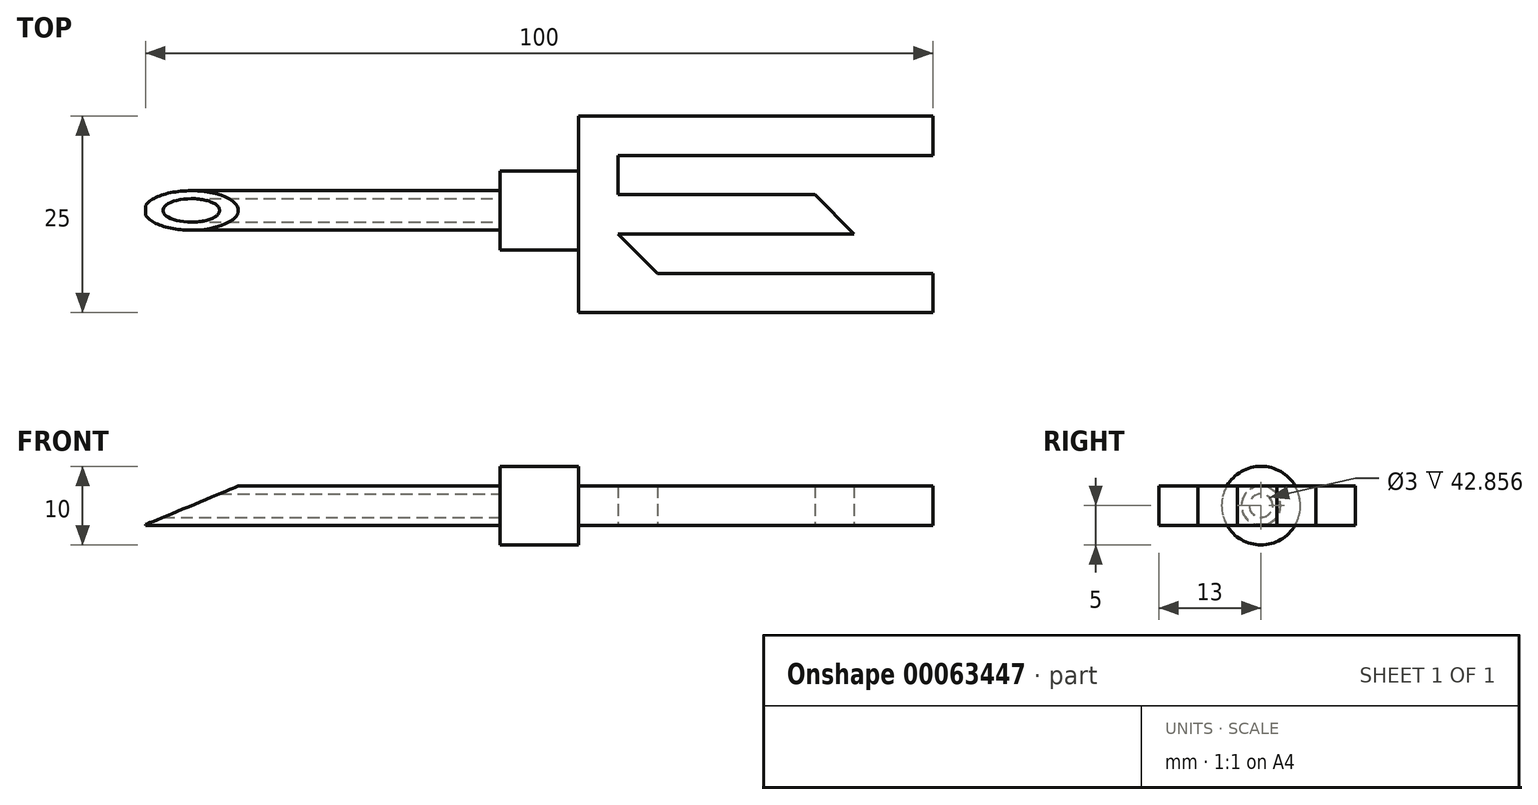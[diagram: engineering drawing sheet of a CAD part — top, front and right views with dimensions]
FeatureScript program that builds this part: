
annotation { "Feature Type Name" : "Feature", "Feature Type Description" : "" }
export const myFeature = defineFeature(function(context is Context, id is Id, definition is map)
    precondition{}
    {
        {
            var Q0;
            Q0=qCreatedBy(makeId("Top.planeOp"),FACE);
            var sketch = newSketch(context, id + "F0", { "sketchPlane" : qUnion([Q0])});
            skLineSegment(sketch, "E0.bottom", {"start": v(0, 0) * mm, "end": v(-45, 0) * mm});
            skLineSegment(sketch, "E0.top", {"start": v(0, 25) * mm, "end": v(-45, 25) * mm});
            skLineSegment(sketch, "E0.left", {"start": v(0, 0) * mm, "end": v(0, 5) * mm});
            skLineSegment(sketch, "E0.right", {"start": v(-45, 0) * mm, "end": v(-45, 25) * mm});
            skLineSegment(sketch, "E1", {"start": v(0, 20) * mm, "end": v(-40, 20) * mm});
            skLineSegment(sketch, "E2", {"start": v(-40, 20) * mm, "end": v(-40, 15) * mm});
            skLineSegment(sketch, "E3", {"start": v(-40, 15) * mm, "end": v(-15, 15) * mm});
            skLineSegment(sketch, "E4", {"start": v(-10, 10) * mm, "end": v(-40, 10) * mm});
            skLineSegment(sketch, "E5", {"start": v(-40, 10) * mm, "end": v(-35, 5) * mm});
            skLineSegment(sketch, "E6", {"start": v(-35, 5) * mm, "end": v(0, 5) * mm});
            skLineSegment(sketch, "E7.trimOffspring", {"start": v(0, 20) * mm, "end": v(0, 25) * mm});
            skLineSegment(sketch, "E8", {"start": v(-15, 15) * mm, "end": v(-10, 10) * mm});
            skSolve(sketch);
        }
        {
            var Q0;
            Q0 = qSketchRegion(id + "F0", true);
            extrude(context, id + "F1", {"entities" : qUnion([Q0]), "depth" : 5 * mm});
        }
        {
            var Q0;
            Q0=makeQuery(id+"F1.opExtrude","SWEPT_FACE",FACE,{"disambiguationData":[OSD([sQuery(id+"F0.wireOp",EDGE,"E0.right")])]});
            var sketch = newSketch(context, id + "F2", { "sketchPlane" : qUnion([Q0])});
            skCircle(sketch, "E9", {"center": v(-13, 2.5) * mm, "radius": 5 * mm});
            skSolve(sketch);
        }
        {
            var Q0;
            Q0 = qSketchRegion(id + "F2", true);
            extrude(context, id + "F3", {"entities" : qUnion([Q0]), "operationType" : NewBodyOperationType.ADD, "depth" : 10 * mm});
        }
        {
            var Q0;
            Q0=makeQuery(id+"F3.opExtrude","CAP_FACE",FACE,{"disambiguationData":[OSD([sQuery(id+"F2.wireOp",EDGE,"E9")])],"isStart":false});
            var sketch = newSketch(context, id + "F4", { "sketchPlane" : qUnion([Q0])});
            skCircle(sketch, "E10", {"center": v(-13, 2.5) * mm, "radius": 2.5 * mm});
            skCircle(sketch, "E11", {"center": v(-13, 2.5) * mm, "radius": 1.5 * mm});
            skSolve(sketch);
        }
        {
            var Q0;
            Q0 = qSketchRegion(id + "F4", true);
            extrude(context, id + "F5", {"entities" : qUnion([Q0]), "operationType" : NewBodyOperationType.ADD, "depth" : 45 * mm});
        }
        {
            var Q0;
            Q0=makeQuery(id+"F1.opExtrude","SWEPT_FACE",FACE,{"disambiguationData":[OSD([sQuery(id+"F0.wireOp",EDGE,"E0.bottom")])]});
            var sketch = newSketch(context, id + "F6", { "sketchPlane" : qUnion([Q0])});
            skLineSegment(sketch, "E12", {"start": v(-100.2, 0) * mm, "end": v(-88.15, 5.02) * mm});
            skLineSegment(sketch, "E13", {"start": v(-88.15, 5.02) * mm, "end": v(-100.2, 5.02) * mm});
            skLineSegment(sketch, "E14", {"start": v(-100.2, 5.02) * mm, "end": v(-100.2, 0) * mm});
            skSolve(sketch);
        }
        {
            var Q0;
            Q0 = qSketchRegion(id + "F6", true);
            extrude(context, id + "F7", {"entities" : qUnion([Q0]), "operationType" : NewBodyOperationType.REMOVE, "oppositeDirection" : true, "depth" : 25 * mm});
        }
    });
